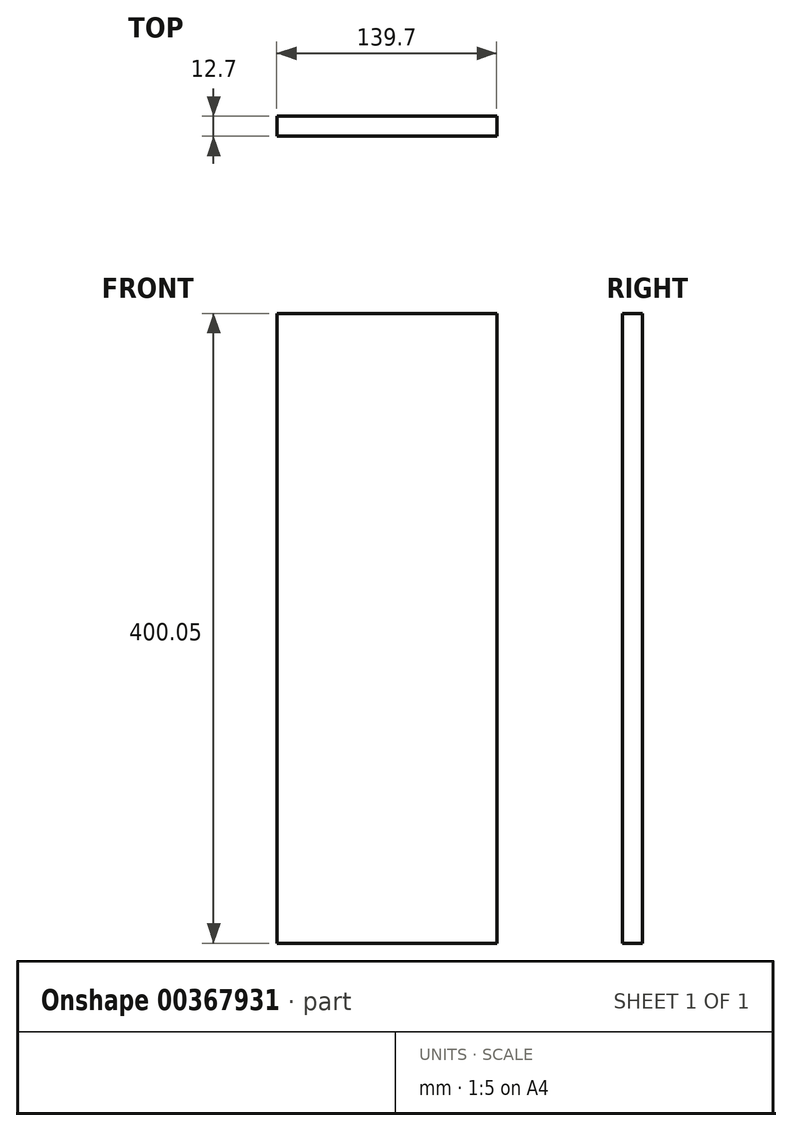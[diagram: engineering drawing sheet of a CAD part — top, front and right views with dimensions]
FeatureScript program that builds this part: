
annotation { "Feature Type Name" : "Feature", "Feature Type Description" : "" }
export const myFeature = defineFeature(function(context is Context, id is Id, definition is map)
    precondition{}
    {
        {
            var Q0;
            Q0=qCreatedBy(makeId("Front.planeOp"),FACE);
            var sketch = newSketch(context, id + "F0", { "sketchPlane" : qUnion([Q0])});
            skLineSegment(sketch, "E0.bottom", {"start": v(-75.94, 327.36) * mm, "end": v(63.76, 327.36) * mm});
            skLineSegment(sketch, "E0.top", {"start": v(-75.94, -72.69) * mm, "end": v(63.76, -72.69) * mm});
            skLineSegment(sketch, "E0.left", {"start": v(-75.94, 327.36) * mm, "end": v(-75.94, -72.69) * mm});
            skLineSegment(sketch, "E0.right", {"start": v(63.76, 327.36) * mm, "end": v(63.76, -72.69) * mm});
            skSolve(sketch);
        }
        {
            var Q0;
            Q0=makeQuery(id+"F0.imprint","IMPRINT",FACE,{"disambiguationData":[TD([[makeQuery(id+"F0.imprint","IMPRINT",EDGE,{"derivedFrom":sQuery(id+"F0.wireOp",EDGE,"E0.bottom")}),-1.0]])]});
            extrude(context, id + "F1", {"entities" : qUnion([Q0]), "depth" : 12.7 * mm});
        }
    });
